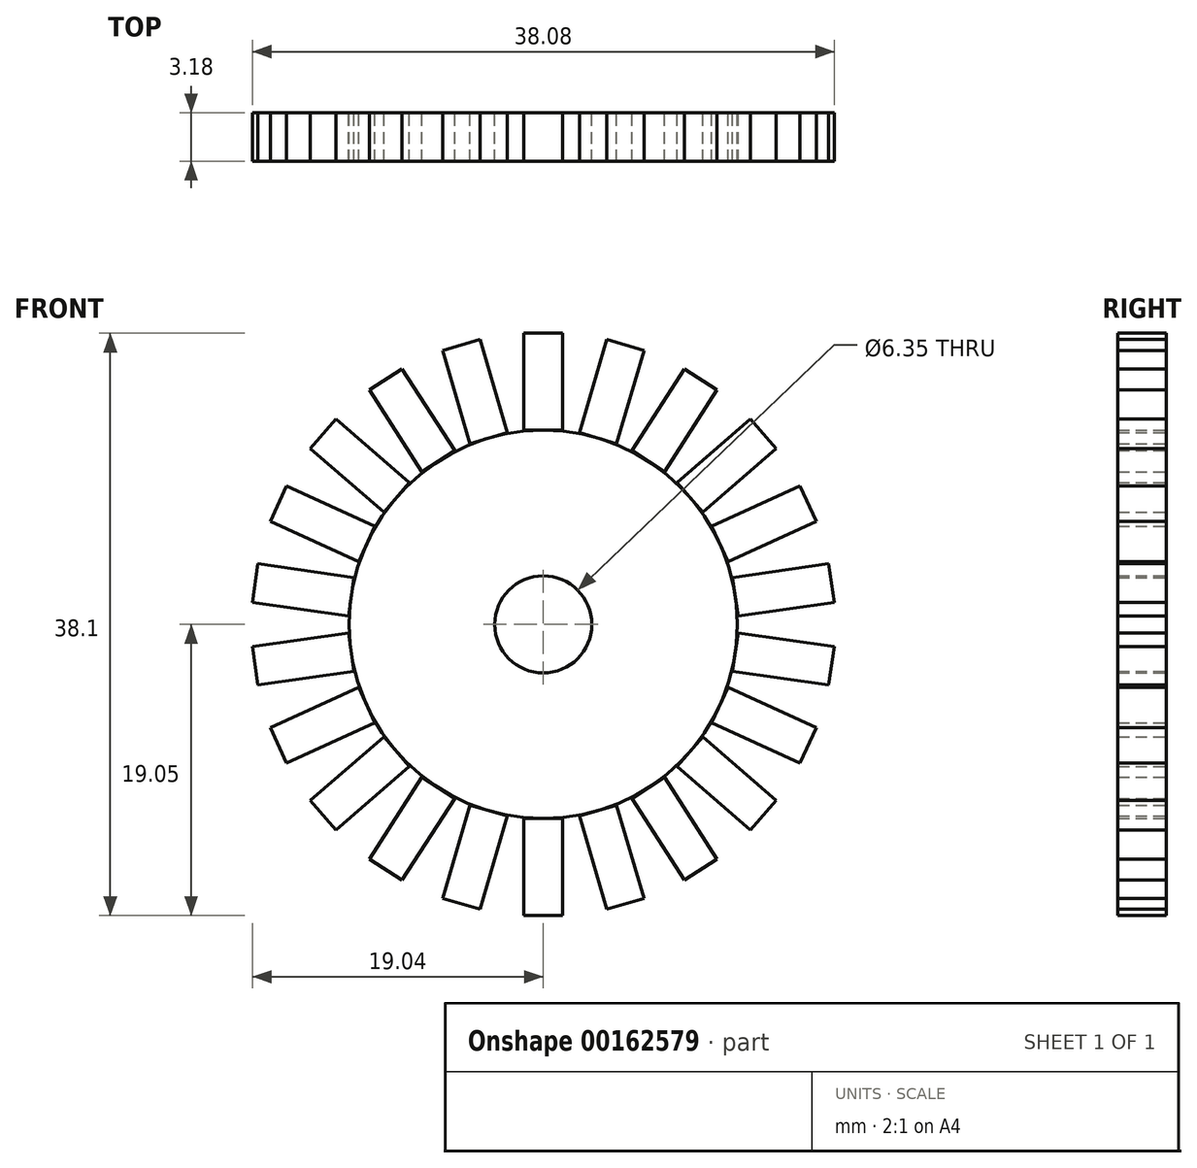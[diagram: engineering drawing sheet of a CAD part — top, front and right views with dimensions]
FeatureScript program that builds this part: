
annotation { "Feature Type Name" : "Feature", "Feature Type Description" : "" }
export const myFeature = defineFeature(function(context is Context, id is Id, definition is map)
    precondition{}
    {
        {
            var Q0;
            Q0=qCreatedBy(makeId("Front.planeOp"),FACE);
            var sketch = newSketch(context, id + "F0", { "sketchPlane" : qUnion([Q0])});
            skCircle(sketch, "E0", {"center": v(0, 0) * mm, "radius": 12.7 * mm});
            skCircle(sketch, "E1", {"center": v(0, 0) * mm, "radius": 3.18 * mm});
            skLineSegment(sketch, "E2.bottom", {"start": v(-1.27, 19.05) * mm, "end": v(1.27, 19.05) * mm});
            skLineSegment(sketch, "E2.top", {"start": v(-1.27, 12.7) * mm, "end": v(1.27, 12.7) * mm});
            skLineSegment(sketch, "E2.left", {"start": v(-1.27, 19.05) * mm, "end": v(-1.27, 12.7) * mm});
            skLineSegment(sketch, "E2.right", {"start": v(1.27, 19.05) * mm, "end": v(1.27, 12.7) * mm});
            skPoint(sketch, "E2.middle", {"position": v(0, 15.88) * mm});
            skLineSegment(sketch, "E3.1.0", {"start": v(-6.59, 17.92) * mm, "end": v(-4.8, 11.83) * mm});
            skLineSegment(sketch, "E3.1.1", {"start": v(-6.59, 17.92) * mm, "end": v(-4.15, 18.64) * mm});
            skLineSegment(sketch, "E3.1.2", {"start": v(-4.15, 18.64) * mm, "end": v(-2.36, 12.54) * mm});
            skLineSegment(sketch, "E3.1.3", {"start": v(-4.8, 11.83) * mm, "end": v(-2.36, 12.54) * mm});
            skLineSegment(sketch, "E3.2.0", {"start": v(-11.37, 15.34) * mm, "end": v(-7.93, 10) * mm});
            skLineSegment(sketch, "E3.2.1", {"start": v(-11.37, 15.34) * mm, "end": v(-9.23, 16.71) * mm});
            skLineSegment(sketch, "E3.2.2", {"start": v(-9.23, 16.71) * mm, "end": v(-5.8, 11.37) * mm});
            skLineSegment(sketch, "E3.2.3", {"start": v(-7.93, 10) * mm, "end": v(-5.8, 11.37) * mm});
            skLineSegment(sketch, "E3.3.0", {"start": v(-15.23, 11.52) * mm, "end": v(-10.43, 7.36) * mm});
            skLineSegment(sketch, "E3.3.1", {"start": v(-15.23, 11.52) * mm, "end": v(-13.57, 13.43) * mm});
            skLineSegment(sketch, "E3.3.2", {"start": v(-13.57, 13.43) * mm, "end": v(-8.77, 9.28) * mm});
            skLineSegment(sketch, "E3.3.3", {"start": v(-10.43, 7.36) * mm, "end": v(-8.77, 9.28) * mm});
            skLineSegment(sketch, "E3.4.0", {"start": v(-17.86, 6.76) * mm, "end": v(-12.08, 4.12) * mm});
            skLineSegment(sketch, "E3.4.1", {"start": v(-17.86, 6.76) * mm, "end": v(-16.8, 9.07) * mm});
            skLineSegment(sketch, "E3.4.2", {"start": v(-16.8, 9.07) * mm, "end": v(-11.02, 6.43) * mm});
            skLineSegment(sketch, "E3.4.3", {"start": v(-12.08, 4.12) * mm, "end": v(-11.02, 6.43) * mm});
            skLineSegment(sketch, "E3.5.0", {"start": v(-19.04, 1.45) * mm, "end": v(-12.75, 0.55) * mm});
            skLineSegment(sketch, "E3.5.1", {"start": v(-19.04, 1.45) * mm, "end": v(-18.68, 3.97) * mm});
            skLineSegment(sketch, "E3.5.2", {"start": v(-18.68, 3.97) * mm, "end": v(-12.39, 3.06) * mm});
            skLineSegment(sketch, "E3.5.3", {"start": v(-12.75, 0.55) * mm, "end": v(-12.39, 3.06) * mm});
            skLineSegment(sketch, "E3.6.0", {"start": v(-18.68, -3.97) * mm, "end": v(-12.39, -3.06) * mm});
            skLineSegment(sketch, "E3.6.1", {"start": v(-18.68, -3.97) * mm, "end": v(-19.04, -1.45) * mm});
            skLineSegment(sketch, "E3.6.2", {"start": v(-19.04, -1.45) * mm, "end": v(-12.75, -0.55) * mm});
            skLineSegment(sketch, "E3.6.3", {"start": v(-12.39, -3.06) * mm, "end": v(-12.75, -0.55) * mm});
            skLineSegment(sketch, "E3.7.0", {"start": v(-16.8, -9.07) * mm, "end": v(-11.02, -6.43) * mm});
            skLineSegment(sketch, "E3.7.1", {"start": v(-16.8, -9.07) * mm, "end": v(-17.86, -6.76) * mm});
            skLineSegment(sketch, "E3.7.2", {"start": v(-17.86, -6.76) * mm, "end": v(-12.08, -4.12) * mm});
            skLineSegment(sketch, "E3.7.3", {"start": v(-11.02, -6.43) * mm, "end": v(-12.08, -4.12) * mm});
            skLineSegment(sketch, "E3.8.0", {"start": v(-13.57, -13.43) * mm, "end": v(-8.77, -9.28) * mm});
            skLineSegment(sketch, "E3.8.1", {"start": v(-13.57, -13.43) * mm, "end": v(-15.23, -11.52) * mm});
            skLineSegment(sketch, "E3.8.2", {"start": v(-15.23, -11.52) * mm, "end": v(-10.43, -7.36) * mm});
            skLineSegment(sketch, "E3.8.3", {"start": v(-8.77, -9.28) * mm, "end": v(-10.43, -7.36) * mm});
            skLineSegment(sketch, "E3.9.0", {"start": v(-9.23, -16.71) * mm, "end": v(-5.8, -11.37) * mm});
            skLineSegment(sketch, "E3.9.1", {"start": v(-9.23, -16.71) * mm, "end": v(-11.37, -15.34) * mm});
            skLineSegment(sketch, "E3.9.2", {"start": v(-11.37, -15.34) * mm, "end": v(-7.93, -10) * mm});
            skLineSegment(sketch, "E3.9.3", {"start": v(-5.8, -11.37) * mm, "end": v(-7.93, -10) * mm});
            skLineSegment(sketch, "E3.10.0", {"start": v(-4.15, -18.64) * mm, "end": v(-2.36, -12.54) * mm});
            skLineSegment(sketch, "E3.10.1", {"start": v(-4.15, -18.64) * mm, "end": v(-6.59, -17.92) * mm});
            skLineSegment(sketch, "E3.10.2", {"start": v(-6.59, -17.92) * mm, "end": v(-4.8, -11.83) * mm});
            skLineSegment(sketch, "E3.10.3", {"start": v(-2.36, -12.54) * mm, "end": v(-4.8, -11.83) * mm});
            skLineSegment(sketch, "E3.11.0", {"start": v(1.27, -19.05) * mm, "end": v(1.27, -12.7) * mm});
            skLineSegment(sketch, "E3.11.1", {"start": v(1.27, -19.05) * mm, "end": v(-1.27, -19.05) * mm});
            skLineSegment(sketch, "E3.11.2", {"start": v(-1.27, -19.05) * mm, "end": v(-1.27, -12.7) * mm});
            skLineSegment(sketch, "E3.11.3", {"start": v(1.27, -12.7) * mm, "end": v(-1.27, -12.7) * mm});
            skLineSegment(sketch, "E3.12.0", {"start": v(6.59, -17.92) * mm, "end": v(4.8, -11.83) * mm});
            skLineSegment(sketch, "E3.12.1", {"start": v(6.59, -17.92) * mm, "end": v(4.15, -18.64) * mm});
            skLineSegment(sketch, "E3.12.2", {"start": v(4.15, -18.64) * mm, "end": v(2.36, -12.54) * mm});
            skLineSegment(sketch, "E3.12.3", {"start": v(4.8, -11.83) * mm, "end": v(2.36, -12.54) * mm});
            skLineSegment(sketch, "E3.13.0", {"start": v(11.37, -15.34) * mm, "end": v(7.93, -10) * mm});
            skLineSegment(sketch, "E3.13.1", {"start": v(11.37, -15.34) * mm, "end": v(9.23, -16.71) * mm});
            skLineSegment(sketch, "E3.13.2", {"start": v(9.23, -16.71) * mm, "end": v(5.8, -11.37) * mm});
            skLineSegment(sketch, "E3.13.3", {"start": v(7.93, -10) * mm, "end": v(5.8, -11.37) * mm});
            skLineSegment(sketch, "E3.14.0", {"start": v(15.23, -11.52) * mm, "end": v(10.43, -7.36) * mm});
            skLineSegment(sketch, "E3.14.1", {"start": v(15.23, -11.52) * mm, "end": v(13.57, -13.43) * mm});
            skLineSegment(sketch, "E3.14.2", {"start": v(13.57, -13.43) * mm, "end": v(8.77, -9.28) * mm});
            skLineSegment(sketch, "E3.14.3", {"start": v(10.43, -7.36) * mm, "end": v(8.77, -9.28) * mm});
            skLineSegment(sketch, "E3.15.0", {"start": v(17.86, -6.76) * mm, "end": v(12.08, -4.12) * mm});
            skLineSegment(sketch, "E3.15.1", {"start": v(17.86, -6.76) * mm, "end": v(16.8, -9.07) * mm});
            skLineSegment(sketch, "E3.15.2", {"start": v(16.8, -9.07) * mm, "end": v(11.02, -6.43) * mm});
            skLineSegment(sketch, "E3.15.3", {"start": v(12.08, -4.12) * mm, "end": v(11.02, -6.43) * mm});
            skLineSegment(sketch, "E3.16.0", {"start": v(19.04, -1.45) * mm, "end": v(12.75, -0.55) * mm});
            skLineSegment(sketch, "E3.16.1", {"start": v(19.04, -1.45) * mm, "end": v(18.68, -3.97) * mm});
            skLineSegment(sketch, "E3.16.2", {"start": v(18.68, -3.97) * mm, "end": v(12.39, -3.06) * mm});
            skLineSegment(sketch, "E3.16.3", {"start": v(12.75, -0.55) * mm, "end": v(12.39, -3.06) * mm});
            skLineSegment(sketch, "E3.17.0", {"start": v(18.68, 3.97) * mm, "end": v(12.39, 3.06) * mm});
            skLineSegment(sketch, "E3.17.1", {"start": v(18.68, 3.97) * mm, "end": v(19.04, 1.45) * mm});
            skLineSegment(sketch, "E3.17.2", {"start": v(19.04, 1.45) * mm, "end": v(12.75, 0.55) * mm});
            skLineSegment(sketch, "E3.17.3", {"start": v(12.39, 3.06) * mm, "end": v(12.75, 0.55) * mm});
            skLineSegment(sketch, "E3.18.0", {"start": v(16.8, 9.07) * mm, "end": v(11.02, 6.43) * mm});
            skLineSegment(sketch, "E3.18.1", {"start": v(16.8, 9.07) * mm, "end": v(17.86, 6.76) * mm});
            skLineSegment(sketch, "E3.18.2", {"start": v(17.86, 6.76) * mm, "end": v(12.08, 4.12) * mm});
            skLineSegment(sketch, "E3.18.3", {"start": v(11.02, 6.43) * mm, "end": v(12.08, 4.12) * mm});
            skLineSegment(sketch, "E3.19.0", {"start": v(13.57, 13.43) * mm, "end": v(8.77, 9.28) * mm});
            skLineSegment(sketch, "E3.19.1", {"start": v(13.57, 13.43) * mm, "end": v(15.23, 11.52) * mm});
            skLineSegment(sketch, "E3.19.2", {"start": v(15.23, 11.52) * mm, "end": v(10.43, 7.36) * mm});
            skLineSegment(sketch, "E3.19.3", {"start": v(8.77, 9.28) * mm, "end": v(10.43, 7.36) * mm});
            skLineSegment(sketch, "E4.2.20.0", {"start": v(9.23, 16.71) * mm, "end": v(5.8, 11.37) * mm});
            skLineSegment(sketch, "E4.3.20.0", {"start": v(9.23, 16.71) * mm, "end": v(11.37, 15.34) * mm});
            skLineSegment(sketch, "E4.6.20.0", {"start": v(11.37, 15.34) * mm, "end": v(7.93, 10) * mm});
            skLineSegment(sketch, "E4.9.20.0", {"start": v(5.8, 11.37) * mm, "end": v(7.93, 10) * mm});
            skLineSegment(sketch, "E4.2.21.0", {"start": v(4.15, 18.64) * mm, "end": v(2.36, 12.54) * mm});
            skLineSegment(sketch, "E4.3.21.0", {"start": v(4.15, 18.64) * mm, "end": v(6.59, 17.92) * mm});
            skLineSegment(sketch, "E4.6.21.0", {"start": v(6.59, 17.92) * mm, "end": v(4.8, 11.83) * mm});
            skLineSegment(sketch, "E4.9.21.0", {"start": v(2.36, 12.54) * mm, "end": v(4.8, 11.83) * mm});
            skSolve(sketch);
        }
        {
            var Q0;
            Q0 = qSketchRegion(id + "F0", true);
            extrude(context, id + "F1", {"entities" : qUnion([Q0]), "depth" : 3.17 * mm});
        }
    });
